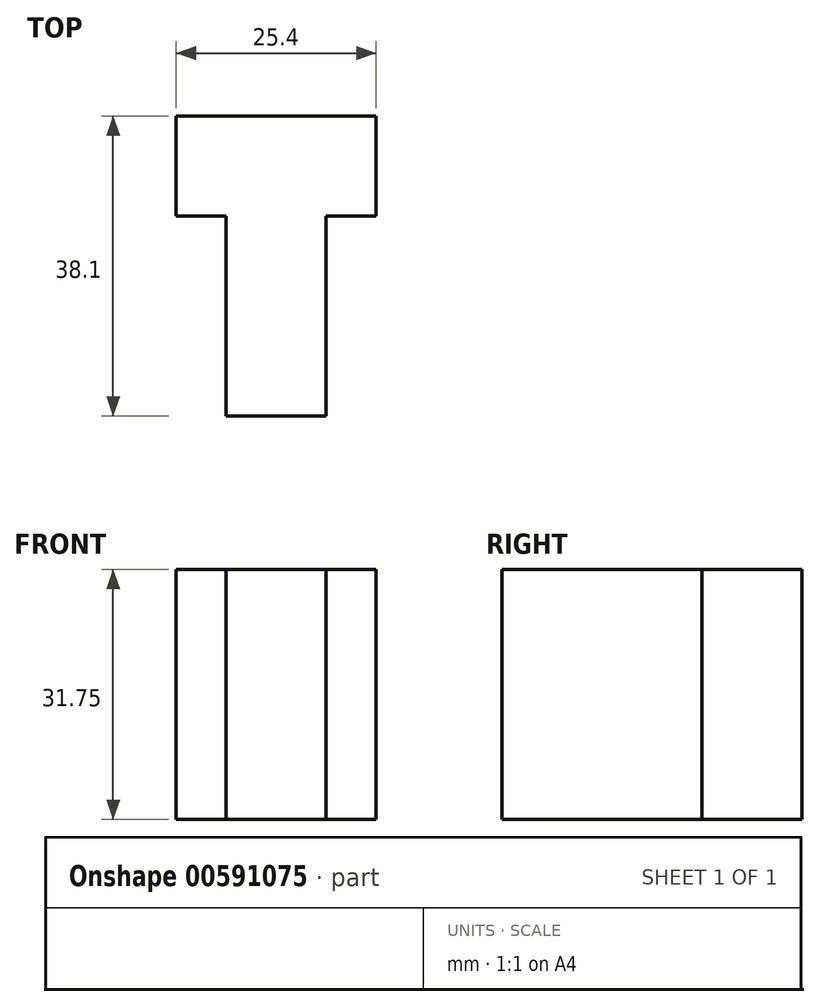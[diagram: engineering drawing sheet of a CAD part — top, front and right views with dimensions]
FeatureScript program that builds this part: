
annotation { "Feature Type Name" : "Feature", "Feature Type Description" : "" }
export const myFeature = defineFeature(function(context is Context, id is Id, definition is map)
    precondition{}
    {
        {
            var Q0;
            Q0=qCreatedBy(makeId("Top.planeOp"),FACE);
            var sketch = newSketch(context, id + "F0", { "sketchPlane" : qUnion([Q0])});
            skLineSegment(sketch, "E0", {"start": v(0, 0) * mm, "end": v(12.7, 0) * mm});
            skLineSegment(sketch, "E1", {"start": v(12.7, 0) * mm, "end": v(12.7, 12.7) * mm});
            skLineSegment(sketch, "E2", {"start": v(12.7, 12.7) * mm, "end": v(-12.7, 12.7) * mm});
            skLineSegment(sketch, "E3", {"start": v(-12.7, 12.7) * mm, "end": v(-12.7, 0) * mm});
            skLineSegment(sketch, "E4", {"start": v(-12.7, 0) * mm, "end": v(0, 0) * mm});
            skLineSegment(sketch, "E5", {"start": v(-6.35, 0) * mm, "end": v(-6.35, -25.4) * mm});
            skLineSegment(sketch, "E6", {"start": v(-6.35, -25.4) * mm, "end": v(6.35, -25.4) * mm});
            skLineSegment(sketch, "E7", {"start": v(6.35, -25.4) * mm, "end": v(6.35, 0) * mm});
            skSolve(sketch);
        }
        {
            var Q0;
            {var subQ0=sQuery(id+"F0.wireOp",EDGE,"E1");Q0=makeQuery(id+"F0.imprint","IMPRINT",FACE,{"disambiguationData":[TD([[makeQuery(id+"F0.imprint","IMPRINT",EDGE,{"derivedFrom":subQ0}),1.0]])]});}
            var Q1;
            {var subQ0=sQuery(id+"F0.wireOp",EDGE,"E5");Q1=makeQuery(id+"F0.imprint","IMPRINT",FACE,{"disambiguationData":[TD([[makeQuery(id+"F0.imprint","IMPRINT",EDGE,{"derivedFrom":subQ0}),1.0]])]});}
            extrude(context, id + "F1", {"entities" : qUnion([Q0, Q1]), "depth" : 31.75 * mm, "offsetDistance" : 25.4 * mm});
        }
    });
